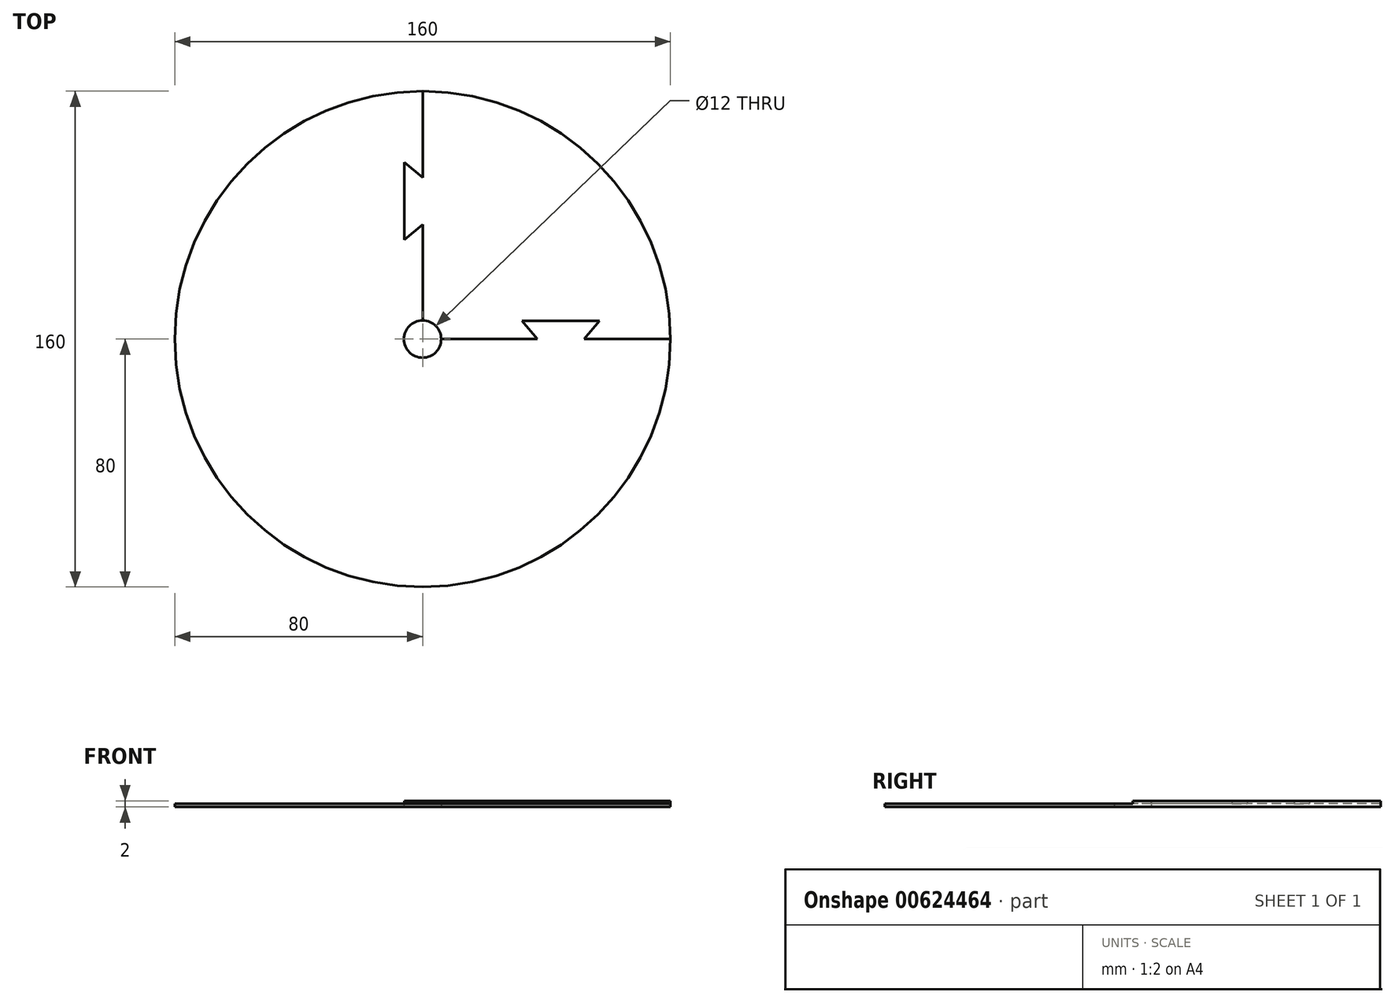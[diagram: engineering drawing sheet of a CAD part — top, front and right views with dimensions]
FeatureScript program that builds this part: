
annotation { "Feature Type Name" : "Feature", "Feature Type Description" : "" }
export const myFeature = defineFeature(function(context is Context, id is Id, definition is map)
    precondition{}
    {
        {
            var Q0;
            Q0=qCreatedBy(makeId("Top.planeOp"),FACE);
            var sketch = newSketch(context, id + "F0", { "sketchPlane" : qUnion([Q0])});
            skCircle(sketch, "E0", {"center": v(0, 0) * mm, "radius": 80 * mm});
            skCircle(sketch, "E1", {"center": v(0, 0) * mm, "radius": 6 * mm});
            skSolve(sketch);
        }
        {
            var Q0;
            Q0 = qSketchRegion(id + "F0", true);
            extrude(context, id + "F1", {"entities" : qUnion([Q0]), "depth" : 1 * mm, "offsetDistance" : 25 * mm});
        }
        {
            var Q0;
            Q0=makeQuery(id+"F1.opExtrude","CAP_FACE",FACE,{"disambiguationData":[OSD([sQuery(id+"F0.wireOp",EDGE,"E0"),sQuery(id+"F0.wireOp",EDGE,"E1")])],"isStart":false});
            var sketch = newSketch(context, id + "F2", { "sketchPlane" : qUnion([Q0])});
            skLineSegment(sketch, "E2", {"start": v(0, 80) * mm, "end": v(0, 52.12) * mm});
            skLineSegment(sketch, "E3", {"start": v(0, 52.12) * mm, "end": v(-5.89, 57.06) * mm});
            skLineSegment(sketch, "E4", {"start": v(-5.89, 57.06) * mm, "end": v(-5.89, 32.06) * mm});
            skLineSegment(sketch, "E5", {"start": v(-5.89, 32.06) * mm, "end": v(0, 37) * mm});
            skLineSegment(sketch, "E6", {"start": v(0, 37) * mm, "end": v(0, 0) * mm});
            skLineSegment(sketch, "E7", {"start": v(0, 0) * mm, "end": v(0, -37) * mm});
            skLineSegment(sketch, "E8", {"start": v(0, -37) * mm, "end": v(5.89, -32.06) * mm});
            skLineSegment(sketch, "E9", {"start": v(5.89, -32.06) * mm, "end": v(5.89, -57.06) * mm});
            skLineSegment(sketch, "E10", {"start": v(5.89, -57.06) * mm, "end": v(0, -52.12) * mm});
            skLineSegment(sketch, "E11", {"start": v(0, -52.12) * mm, "end": v(0, -80) * mm});
            skLineSegment(sketch, "E12", {"start": v(0, 0) * mm, "end": v(37, 0) * mm});
            skLineSegment(sketch, "E13", {"start": v(37, 0) * mm, "end": v(32.06, 5.89) * mm});
            skLineSegment(sketch, "E14", {"start": v(32.06, 5.89) * mm, "end": v(57.06, 5.89) * mm});
            skLineSegment(sketch, "E15", {"start": v(57.06, 5.89) * mm, "end": v(52.12, 0) * mm});
            skLineSegment(sketch, "E16", {"start": v(52.12, 0) * mm, "end": v(80, 0) * mm});
            skLineSegment(sketch, "E17", {"start": v(0, 0) * mm, "end": v(-37, 0) * mm});
            skLineSegment(sketch, "E18", {"start": v(-37, 0) * mm, "end": v(-32.06, -5.89) * mm});
            skLineSegment(sketch, "E19", {"start": v(-32.06, -5.89) * mm, "end": v(-57.06, -5.89) * mm});
            skLineSegment(sketch, "E20", {"start": v(-57.06, -5.89) * mm, "end": v(-52.12, 0) * mm});
            skLineSegment(sketch, "E21", {"start": v(-52.12, 0) * mm, "end": v(-80, 0) * mm});
            skSolve(sketch);
        }
        {
            var Q0;
            {var subQ5=sQuery(id+"F2.wireOp",EDGE,"E2");Q0=makeQuery(id+"F2.imprint","IMPRINT",FACE,{"disambiguationData":[TD([[makeQuery(id+"F2.imprint","IMPRINT",EDGE,{"derivedFrom":subQ5}),1.0]])]});}
            extrude(context, id + "F3", {"entities" : qUnion([Q0]), "operationType" : NewBodyOperationType.ADD, "depth" : 1 * mm, "offsetDistance" : 25 * mm});
        }
    });
